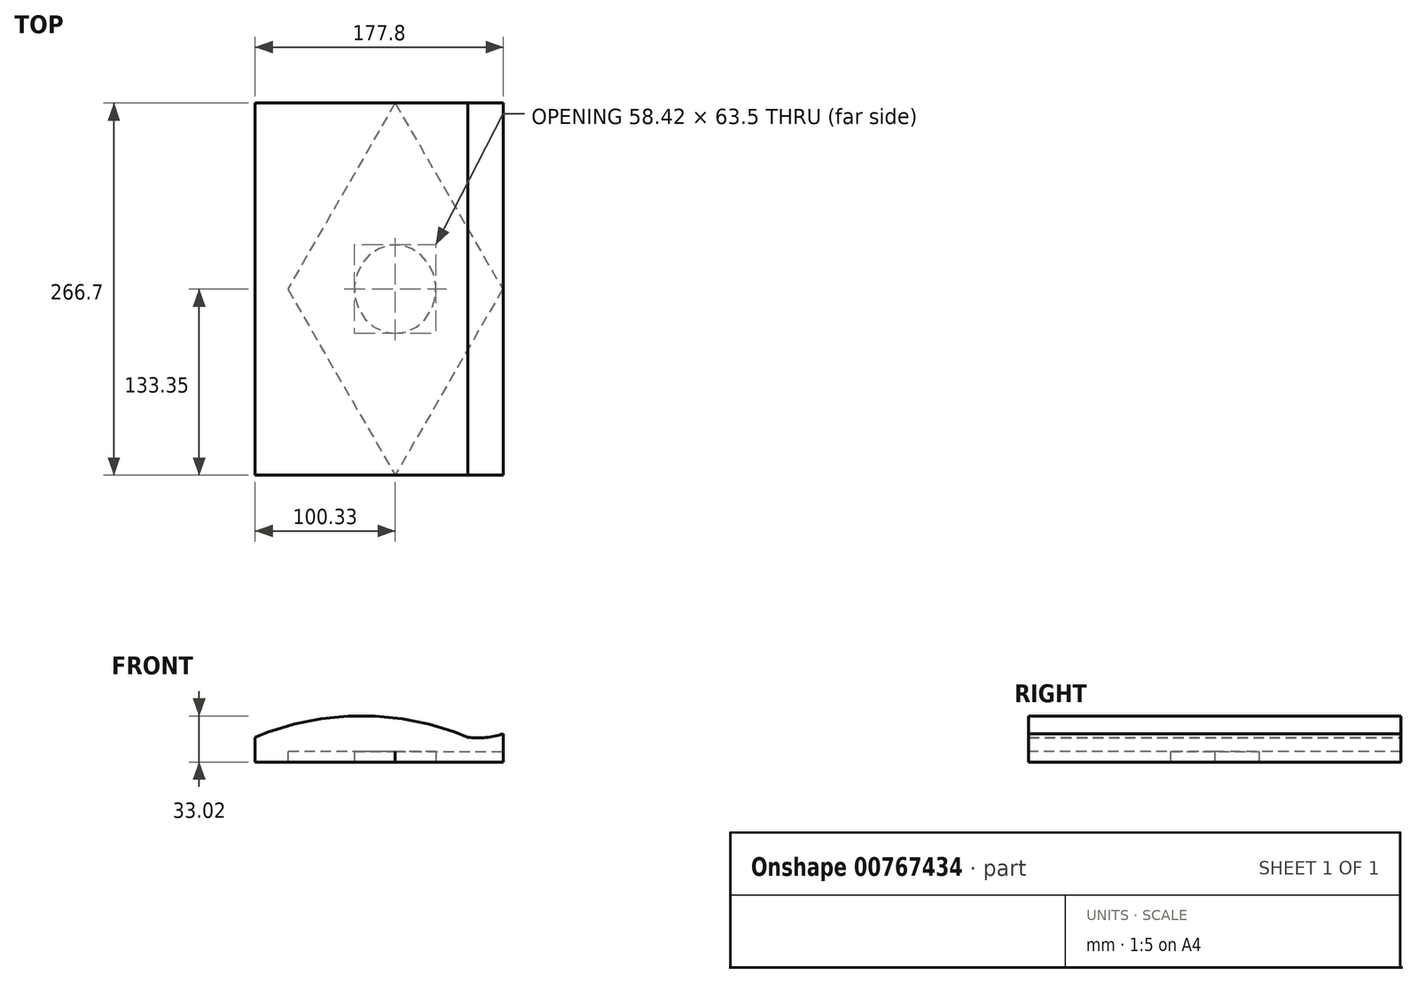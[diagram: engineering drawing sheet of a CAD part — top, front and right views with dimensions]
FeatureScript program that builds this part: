
annotation { "Feature Type Name" : "Feature", "Feature Type Description" : "" }
export const myFeature = defineFeature(function(context is Context, id is Id, definition is map)
    precondition{}
    {
        {
            var Q0;
            Q0=qCreatedBy(makeId("Front.planeOp"),FACE);
            var sketch = newSketch(context, id + "F0", { "sketchPlane" : qUnion([Q0])});
            skArc(sketch, "E0", {"start": v(22.86, 17.78) * mm, "mid": v(-53.34, 33.02) * mm, "end": v(-129.54, 17.78) * mm});
            skArc(sketch, "E1", {"start": v(22.86, 17.78) * mm, "mid": v(35.71, 17.52) * mm, "end": v(48.26, 20.32) * mm});
            skLineSegment(sketch, "E2", {"start": v(-129.54, 17.78) * mm, "end": v(-129.54, 0) * mm});
            skLineSegment(sketch, "E3", {"start": v(-129.54, 0) * mm, "end": v(48.26, 0) * mm});
            skLineSegment(sketch, "E4", {"start": v(48.26, 0) * mm, "end": v(48.26, 20.32) * mm});
            skLineSegment(sketch, "E5", {"start": v(0, 25.7) * mm, "end": v(0, 0) * mm});
            skLineSegment(sketch, "E6", {"start": v(-53.34, 33.02) * mm, "end": v(-53.34, 0) * mm});
            skLineSegment(sketch, "E7", {"start": v(35.71, 17.52) * mm, "end": v(35.71, 0) * mm});
            skArc(sketch, "E8", {"start": v(22.86, 130.11) * mm, "mid": v(35.71, 129.85) * mm, "end": v(48.26, 132.65) * mm});
            skArc(sketch, "E9", {"start": v(22.86, 130.11) * mm, "mid": v(-53.34, 145.35) * mm, "end": v(-129.54, 130.11) * mm});
            skLineSegment(sketch, "E10", {"start": v(48.26, 132.65) * mm, "end": v(48.26, 152.97) * mm});
            skLineSegment(sketch, "E11", {"start": v(48.26, 152.97) * mm, "end": v(-129.54, 152.97) * mm});
            skLineSegment(sketch, "E12", {"start": v(-129.54, 152.97) * mm, "end": v(-129.54, 130.11) * mm});
            skSolve(sketch);
        }
        {
            var Q0;
            Q0=makeQuery(id+"F0.imprint","IMPRINT",FACE,{"disambiguationData":[TD([[makeQuery(id+"F0.imprint","IMPRINT",EDGE,{"derivedFrom":sQuery(id+"F0.wireOp",EDGE,"E0")}),1.0]])]});
            var Q1;
            {var subQ1=sQuery(id+"F0.wireOp",EDGE,"E1");Q1=makeQuery(id+"F0.imprint","IMPRINT",FACE,{"disambiguationData":[TD([[makeQuery(id+"F0.imprint","IMPRINT",EDGE,{"derivedFrom":subQ1}),-1.0]])]});}
            var Q2;
            {var subQ0=sQuery(id+"F0.wireOp",EDGE,"E5");Q2=makeQuery(id+"F0.imprint","IMPRINT",FACE,{"disambiguationData":[TD([[makeQuery(id+"F0.imprint","IMPRINT",EDGE,{"derivedFrom":subQ0}),1.0]])]});}
            extrude(context, id + "F1", {"entities" : qUnion([Q0, Q1, Q2]), "depth" : 266.7 * mm, "offsetDistance" : 25.4 * mm});
        }
        {
            var Q0;
            Q0=makeQuery(id+"F0.imprint","IMPRINT",FACE,{"disambiguationData":[TD([[makeQuery(id+"F0.imprint","IMPRINT",EDGE,{"derivedFrom":sQuery(id+"F0.wireOp",EDGE,"E0")}),1.0]])]});
            extrude(context, id + "F2", {"entities" : qUnion([Q0]), "operationType" : NewBodyOperationType.ADD, "depth" : 266.7 * mm, "offsetDistance" : 25.4 * mm});
        }
        {
            var Q0;
            Q0=qCreatedBy(makeId("Top.planeOp"),FACE);
            var sketch = newSketch(context, id + "F3", { "sketchPlane" : qUnion([Q0])});
            skLineSegment(sketch, "E13", {"start": v(-29.2, 0) * mm, "end": v(47.78, -133.35) * mm});
            skLineSegment(sketch, "E14", {"start": v(-29.2, 0) * mm, "end": v(-106.2, -133.35) * mm});
            skLineSegment(sketch, "E15", {"start": v(-106.2, -133.35) * mm, "end": v(-29.2, -266.7) * mm});
            skLineSegment(sketch, "E16", {"start": v(47.78, -133.35) * mm, "end": v(-29.2, -266.7) * mm});
            skEllipse(sketch, "E17", {"center": v(-29.2, -133.35) * mm, "majorRadius": 31.75 * mm, "minorRadius": 29.21 * mm, "majorAxis": v(0, -1)});
            skSolve(sketch);
        }
        {
            var Q0;
            Q0=makeQuery(id+"F3.imprint","IMPRINT",FACE,{"disambiguationData":[TD([[makeQuery(id+"F3.imprint","IMPRINT",EDGE,{"derivedFrom":sQuery(id+"F3.wireOp",EDGE,"E13")}),-1.0]])]});
            extrude(context, id + "F4", {"entities" : qUnion([Q0]), "depth" : 7.62 * mm, "offsetDistance" : 25.4 * mm});
        }
    });
